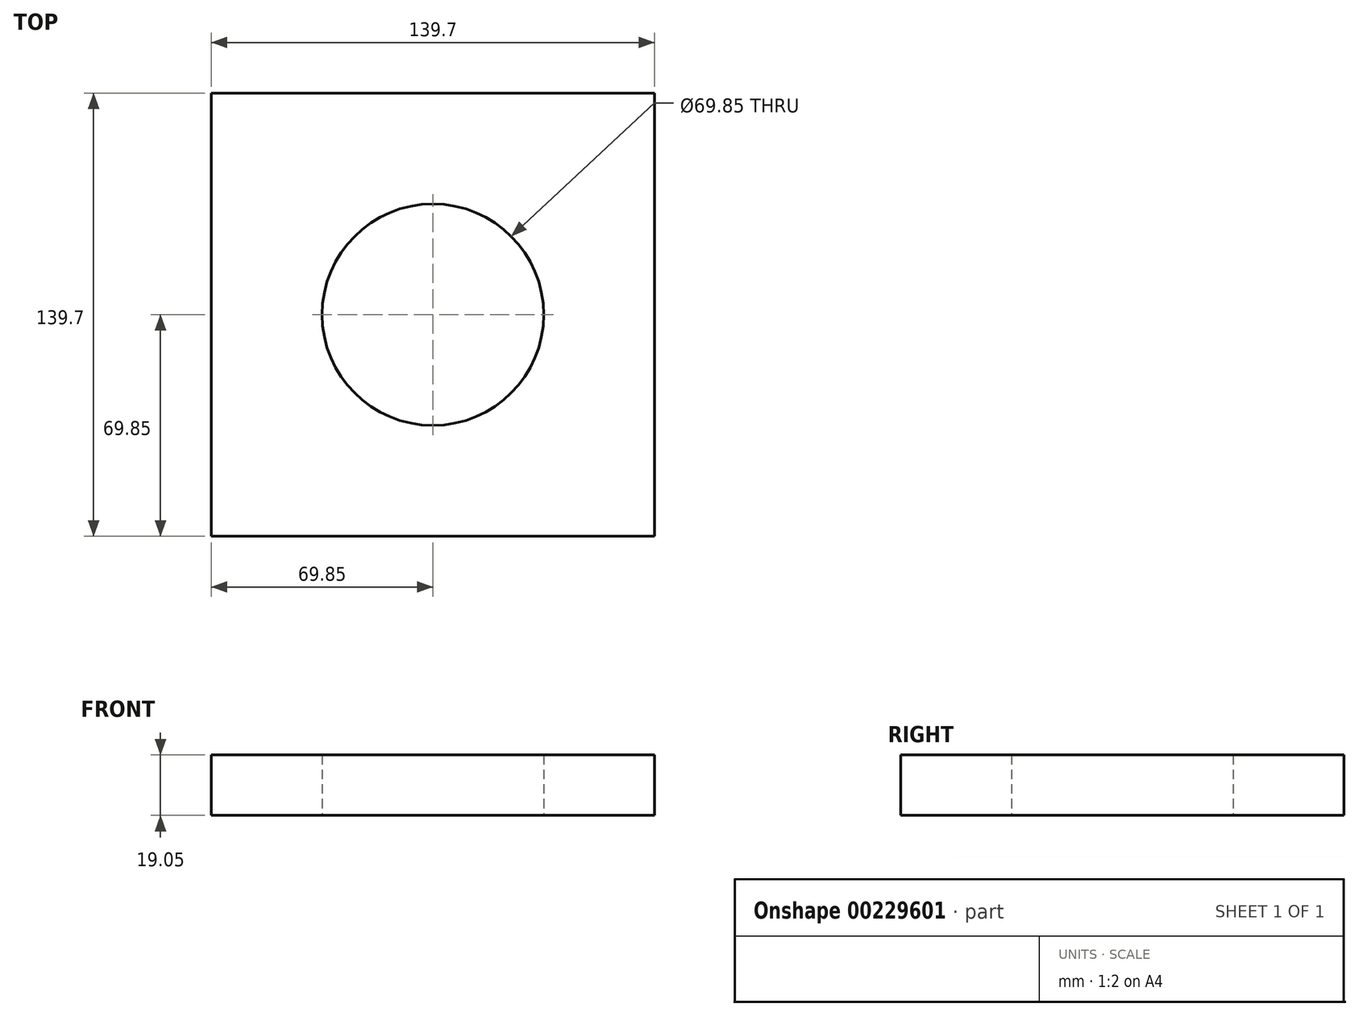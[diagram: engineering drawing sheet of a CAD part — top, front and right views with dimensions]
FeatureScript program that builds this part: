
annotation { "Feature Type Name" : "Feature", "Feature Type Description" : "" }
export const myFeature = defineFeature(function(context is Context, id is Id, definition is map)
    precondition{}
    {
        {
            var Q0;
            Q0=qCreatedBy(makeId("Top.planeOp"),FACE);
            var sketch = newSketch(context, id + "F0", { "sketchPlane" : qUnion([Q0])});
            skLineSegment(sketch, "E0.bottom", {"start": v(69.85, -69.85) * mm, "end": v(-69.85, -69.85) * mm});
            skLineSegment(sketch, "E0.top", {"start": v(69.85, 69.85) * mm, "end": v(-69.85, 69.85) * mm});
            skLineSegment(sketch, "E0.left", {"start": v(69.85, -69.85) * mm, "end": v(69.85, 69.85) * mm});
            skLineSegment(sketch, "E0.right", {"start": v(-69.85, -69.85) * mm, "end": v(-69.85, 69.85) * mm});
            skPoint(sketch, "E0.middle", {"position": v(0, 0) * mm});
            skCircle(sketch, "E1", {"center": v(0, 0) * mm, "radius": 34.93 * mm});
            skSolve(sketch);
        }
        {
            var Q0;
            Q0 = qSketchRegion(id + "F0", true);
            extrude(context, id + "F1", {"entities" : qUnion([Q0]), "depth" : 19.05 * mm});
        }
    });
